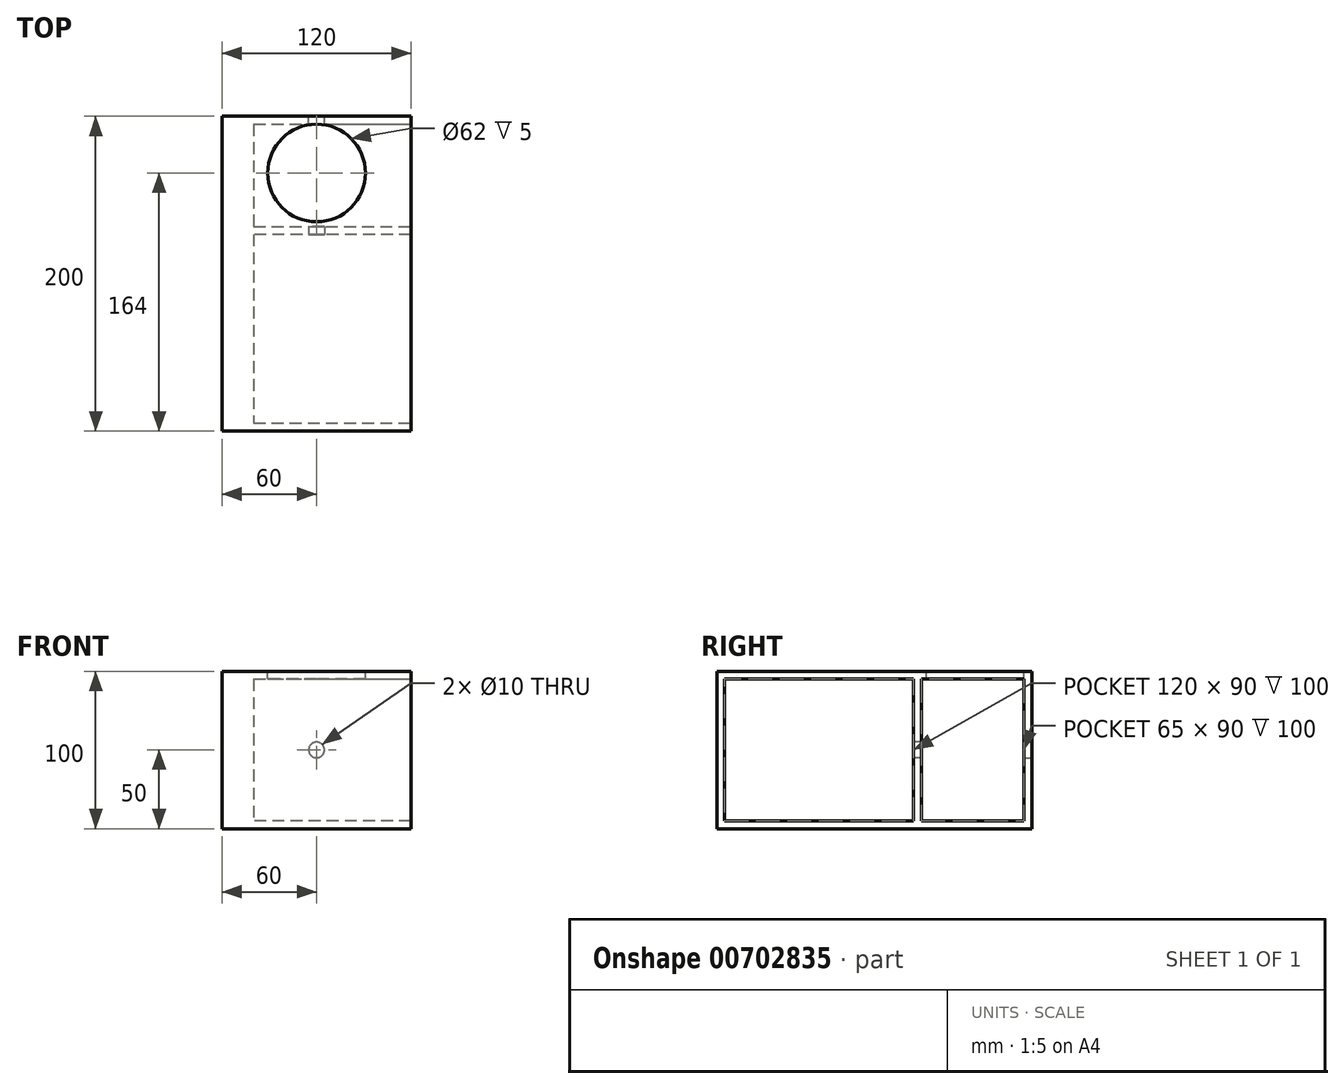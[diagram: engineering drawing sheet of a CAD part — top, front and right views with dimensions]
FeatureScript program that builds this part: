
annotation { "Feature Type Name" : "Feature", "Feature Type Description" : "" }
export const myFeature = defineFeature(function(context is Context, id is Id, definition is map)
    precondition{}
    {
        {
            var Q0;
            Q0=qCreatedBy(makeId("Top.planeOp"),FACE);
            var sketch = newSketch(context, id + "F0", { "sketchPlane" : qUnion([Q0])});
            skLineSegment(sketch, "E0.bottom", {"start": v(60, 100) * mm, "end": v(-60, 100) * mm});
            skLineSegment(sketch, "E0.top", {"start": v(60, -100) * mm, "end": v(-60, -100) * mm});
            skLineSegment(sketch, "E0.left", {"start": v(60, 100) * mm, "end": v(60, -100) * mm});
            skLineSegment(sketch, "E0.right", {"start": v(-60, 100) * mm, "end": v(-60, -100) * mm});
            skPoint(sketch, "E0.middle", {"position": v(0, 0) * mm});
            skLineSegment(sketch, "E1.bottom", {"start": v(60, 25) * mm, "end": v(-60, 25) * mm});
            skLineSegment(sketch, "E1.top", {"start": v(60, 30) * mm, "end": v(-60, 30) * mm});
            skLineSegment(sketch, "E1.left", {"start": v(60, 25) * mm, "end": v(60, 30) * mm});
            skLineSegment(sketch, "E1.right", {"start": v(-60, 25) * mm, "end": v(-60, 30) * mm});
            skSolve(sketch);
        }
        {
            var Q0;
            Q0 = qSketchRegion(id + "F0", true);
            extrude(context, id + "F1", {"entities" : qUnion([Q0]), "oppositeDirection" : true, "depth" : 50 * mm, "offsetDistance" : 25.4 * mm});
        }
        {
            var Q0;
            Q0 = qSketchRegion(id + "F0", true);
            extrude(context, id + "F2", {"entities" : qUnion([Q0]), "operationType" : NewBodyOperationType.ADD, "depth" : 50 * mm, "offsetDistance" : 25 * mm});
        }
        {
            var Q0;
            {var subQ0=sQuery(id+"F0.wireOp",EDGE,"E0.left");Q0=makeQuery(id+"F2.boolean.opBoolean","MERGE",FACE,{"derivedFrom":[makeQuery(id+"F1.opExtrude","SWEPT_FACE",FACE,{"disambiguationData":[OSD([subQ0])]}),makeQuery(id+"F2.opExtrude","SWEPT_FACE",FACE,{"disambiguationData":[OSD([subQ0])]})]});}
            var sketch = newSketch(context, id + "F3", { "sketchPlane" : qUnion([Q0])});
            skLineSegment(sketch, "E2.bottom", {"start": v(95, 45) * mm, "end": v(-95, 45) * mm});
            skLineSegment(sketch, "E2.top", {"start": v(95, -45) * mm, "end": v(-95, -45) * mm});
            skLineSegment(sketch, "E2.left", {"start": v(95, 45) * mm, "end": v(95, -45) * mm});
            skLineSegment(sketch, "E2.right", {"start": v(-95, 45) * mm, "end": v(-95, -45) * mm});
            skPoint(sketch, "E2.middle", {"position": v(0, 0) * mm});
            skSolve(sketch);
        }
        {
            var Q0;
            Q0 = qSketchRegion(id + "F3", true);
            extrude(context, id + "F4", {"entities" : qUnion([Q0]), "operationType" : NewBodyOperationType.REMOVE, "oppositeDirection" : true, "depth" : 100 * mm, "offsetDistance" : 25 * mm});
        }
        {
            var Q0;
            Q0=makeQuery(id+"F2.opExtrude","CAP_FACE",FACE,{"disambiguationData":[OSD([sQuery(id+"F0.wireOp",EDGE,"E0.bottom"),sQuery(id+"F0.wireOp",EDGE,"E0.top"),sQuery(id+"F0.wireOp",EDGE,"E0.left"),sQuery(id+"F0.wireOp",EDGE,"E0.right")])],"isStart":false});
            var sketch = newSketch(context, id + "F5", { "sketchPlane" : qUnion([Q0])});
            skCircle(sketch, "E3", {"center": v(0, 64) * mm, "radius": 31 * mm});
            skSolve(sketch);
        }
        {
            var Q0;
            Q0 = qSketchRegion(id + "F5", true);
            extrude(context, id + "F6", {"entities" : qUnion([Q0]), "operationType" : NewBodyOperationType.REMOVE, "oppositeDirection" : true, "depth" : 25 * mm, "offsetDistance" : 25 * mm});
        }
        {
            var Q0;
            {var subQ0=sQuery(id+"F0.wireOp",EDGE,"E0.bottom");Q0=makeQuery(id+"F2.boolean.opBoolean","MERGE",FACE,{"derivedFrom":[makeQuery(id+"F1.opExtrude","SWEPT_FACE",FACE,{"disambiguationData":[OSD([subQ0])]}),makeQuery(id+"F2.opExtrude","SWEPT_FACE",FACE,{"disambiguationData":[OSD([subQ0])]})]});}
            var sketch = newSketch(context, id + "F7", { "sketchPlane" : qUnion([Q0])});
            skCircle(sketch, "E4", {"center": v(0, 0) * mm, "radius": 5 * mm});
            skSolve(sketch);
        }
        {
            var Q0;
            Q0 = qSketchRegion(id + "F7", true);
            extrude(context, id + "F8", {"entities" : qUnion([Q0]), "operationType" : NewBodyOperationType.REMOVE, "oppositeDirection" : true, "depth" : 25 * mm, "offsetDistance" : 25 * mm});
        }
        {
            var Q0;
            Q0=makeQuery(id+"F0.imprint","IMPRINT",FACE,{"disambiguationData":[TD([[makeQuery(id+"F0.imprint","IMPRINT",EDGE,{"derivedFrom":sQuery(id+"F0.wireOp",EDGE,"E1.bottom")}),-1.0]])]});
            extrude(context, id + "F9", {"entities" : qUnion([Q0]), "operationType" : NewBodyOperationType.ADD, "depth" : 50 * mm, "offsetDistance" : 25 * mm});
        }
        {
            var Q0;
            Q0=makeQuery(id+"F0.imprint","IMPRINT",FACE,{"disambiguationData":[TD([[makeQuery(id+"F0.imprint","IMPRINT",EDGE,{"derivedFrom":sQuery(id+"F0.wireOp",EDGE,"E1.bottom")}),-1.0]])]});
            extrude(context, id + "F10", {"entities" : qUnion([Q0]), "operationType" : NewBodyOperationType.ADD, "oppositeDirection" : true, "depth" : 50 * mm, "offsetDistance" : 25 * mm});
        }
        {
            var Q0;
            {var subQ0=sQuery(id+"F0.wireOp",EDGE,"E1.bottom");Q0=makeQuery(id+"F10.boolean.opBoolean","MERGE",FACE,{"derivedFrom":[makeQuery(id+"F9.opExtrude","SWEPT_FACE",FACE,{"disambiguationData":[OSD([subQ0])]}),makeQuery(id+"F10.opExtrude","SWEPT_FACE",FACE,{"disambiguationData":[OSD([subQ0])]})]});}
            var sketch = newSketch(context, id + "F11", { "sketchPlane" : qUnion([Q0])});
            skCircle(sketch, "E5", {"center": v(0, 0) * mm, "radius": 5 * mm});
            skSolve(sketch);
        }
        {
            var Q0;
            Q0 = qSketchRegion(id + "F11", true);
            extrude(context, id + "F12", {"entities" : qUnion([Q0]), "operationType" : NewBodyOperationType.REMOVE, "oppositeDirection" : true, "depth" : 25 * mm, "offsetDistance" : 25 * mm});
        }
    });
